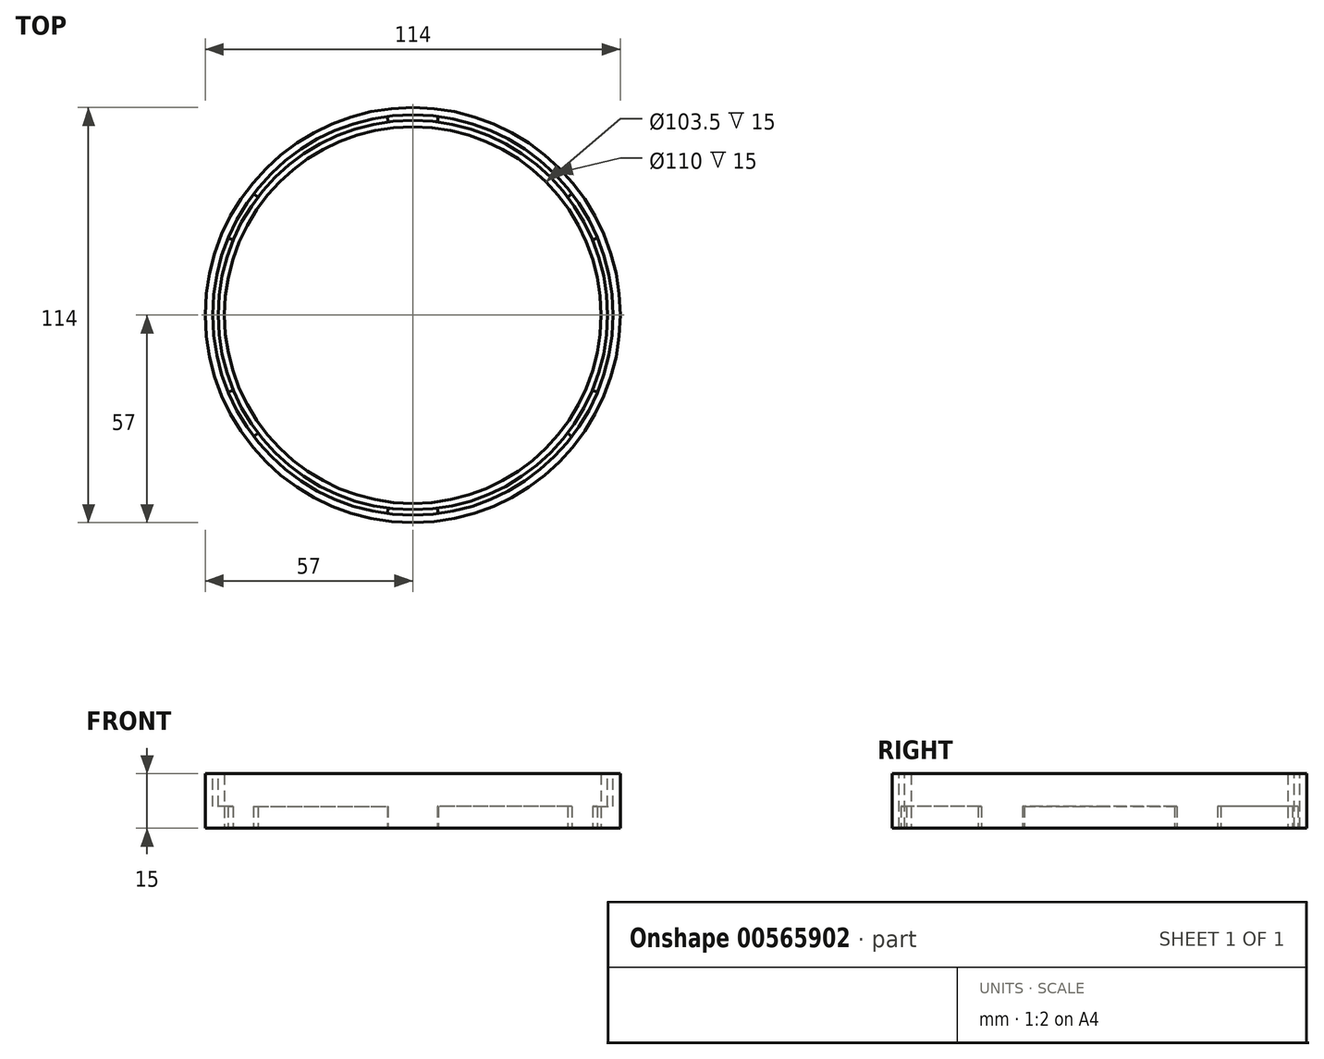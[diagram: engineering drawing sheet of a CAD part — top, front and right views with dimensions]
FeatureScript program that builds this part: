
annotation { "Feature Type Name" : "Feature", "Feature Type Description" : "" }
export const myFeature = defineFeature(function(context is Context, id is Id, definition is map)
    precondition{}
    {
        {
            var Q0;
            Q0=qCreatedBy(makeId("Top.planeOp"),FACE);
            var sketch = newSketch(context, id + "F0", { "sketchPlane" : qUnion([Q0])});
            skCircle(sketch, "E0", {"center": v(0, 0) * mm, "radius": 51.75 * mm});
            skCircle(sketch, "E1", {"center": v(0, 0) * mm, "radius": 57 * mm});
            skSolve(sketch);
        }
        {
            var Q0;
            Q0 = qSketchRegion(id + "F0", true);
            extrude(context, id + "F1", {"entities" : qUnion([Q0]), "depth" : 15 * mm, "offsetDistance" : 25 * mm});
        }
        {
            var Q0;
            Q0=makeQuery(id+"F1.opExtrude","CAP_FACE",FACE,{"disambiguationData":[OSD([sQuery(id+"F0.wireOp",EDGE,"E0"),sQuery(id+"F0.wireOp",EDGE,"E1")])],"isStart":false});
            var sketch = newSketch(context, id + "F2", { "sketchPlane" : qUnion([Q0])});
            skCircle(sketch, "E2", {"center": v(0, 0) * mm, "radius": 53.5 * mm});
            skCircle(sketch, "E3", {"center": v(0, 0) * mm, "radius": 55 * mm});
            skSolve(sketch);
        }
        {
            var Q0;
            Q0 = qSketchRegion(id + "F2", true);
            extrude(context, id + "F3", {"entities" : qUnion([Q0]), "operationType" : NewBodyOperationType.REMOVE, "oppositeDirection" : true, "depth" : 9 * mm, "offsetDistance" : 25 * mm});
        }
        {
            var Q0;
            Q0=qCreatedBy(makeId("Top.planeOp"),FACE);
            var sketch = newSketch(context, id + "F4", { "sketchPlane" : qUnion([Q0])});
            skArc(sketch, "E4.0", {"start": v(-7, -54.55) * mm, "mid": v(0, -55) * mm, "end": v(7, -54.55) * mm});
            skArc(sketch, "E4.1", {"start": v(-6.8, -53.06) * mm, "mid": v(0, -53.5) * mm, "end": v(6.8, -53.06) * mm});
            skLineSegment(sketch, "E5", {"start": v(6.8, -53.06) * mm, "end": v(7, -54.55) * mm});
            skLineSegment(sketch, "E6", {"start": v(-6.8, -53.06) * mm, "end": v(-7, -54.55) * mm});
            skLineSegment(sketch, "E7", {"start": v(0, -55) * mm, "end": v(7, -54.55) * mm, "construction": true});
            skLineSegment(sketch, "E8", {"start": v(-7, -54.55) * mm, "end": v(0, -55) * mm, "construction": true});
            skArc(sketch, "E9.1.0", {"start": v(42.55, -32.43) * mm, "mid": v(46.33, -26.75) * mm, "end": v(49.36, -20.64) * mm});
            skLineSegment(sketch, "E9.1.1", {"start": v(49.36, -20.64) * mm, "end": v(50.74, -21.21) * mm});
            skArc(sketch, "E9.1.2", {"start": v(43.74, -33.34) * mm, "mid": v(47.63, -27.5) * mm, "end": v(50.74, -21.21) * mm});
            skLineSegment(sketch, "E9.1.3", {"start": v(42.55, -32.43) * mm, "end": v(43.74, -33.34) * mm});
            skArc(sketch, "E9.2.0", {"start": v(49.36, 20.64) * mm, "mid": v(46.33, 26.75) * mm, "end": v(42.55, 32.43) * mm});
            skLineSegment(sketch, "E9.2.1", {"start": v(42.55, 32.43) * mm, "end": v(43.74, 33.34) * mm});
            skArc(sketch, "E9.2.2", {"start": v(50.74, 21.21) * mm, "mid": v(47.63, 27.5) * mm, "end": v(43.74, 33.34) * mm});
            skLineSegment(sketch, "E9.2.3", {"start": v(49.36, 20.64) * mm, "end": v(50.74, 21.21) * mm});
            skArc(sketch, "E9.3.0", {"start": v(6.8, 53.06) * mm, "mid": v(0, 53.5) * mm, "end": v(-6.8, 53.06) * mm});
            skLineSegment(sketch, "E9.3.1", {"start": v(-6.8, 53.06) * mm, "end": v(-7, 54.55) * mm});
            skArc(sketch, "E9.3.2", {"start": v(7, 54.55) * mm, "mid": v(0, 55) * mm, "end": v(-7, 54.55) * mm});
            skLineSegment(sketch, "E9.3.3", {"start": v(6.8, 53.06) * mm, "end": v(7, 54.55) * mm});
            skArc(sketch, "E9.4.0", {"start": v(-42.55, 32.43) * mm, "mid": v(-46.33, 26.75) * mm, "end": v(-49.36, 20.64) * mm});
            skLineSegment(sketch, "E9.4.1", {"start": v(-49.36, 20.64) * mm, "end": v(-50.74, 21.21) * mm});
            skArc(sketch, "E9.4.2", {"start": v(-43.74, 33.34) * mm, "mid": v(-47.63, 27.5) * mm, "end": v(-50.74, 21.21) * mm});
            skLineSegment(sketch, "E9.4.3", {"start": v(-42.55, 32.43) * mm, "end": v(-43.74, 33.34) * mm});
            skArc(sketch, "E9.5.0", {"start": v(-49.36, -20.64) * mm, "mid": v(-46.33, -26.75) * mm, "end": v(-42.55, -32.43) * mm});
            skLineSegment(sketch, "E9.5.1", {"start": v(-42.55, -32.43) * mm, "end": v(-43.74, -33.34) * mm});
            skArc(sketch, "E9.5.2", {"start": v(-50.74, -21.21) * mm, "mid": v(-47.63, -27.5) * mm, "end": v(-43.74, -33.34) * mm});
            skLineSegment(sketch, "E9.5.3", {"start": v(-49.36, -20.64) * mm, "end": v(-50.74, -21.21) * mm});
            skSolve(sketch);
        }
        {
            var Q0;
            Q0 = qSketchRegion(id + "F4", true);
            extrude(context, id + "F5", {"entities" : qUnion([Q0]), "operationType" : NewBodyOperationType.REMOVE, "endBound" : BoundingType.THROUGH_ALL, "depth" : 25 * mm, "offsetDistance" : 25 * mm});
        }
    });
